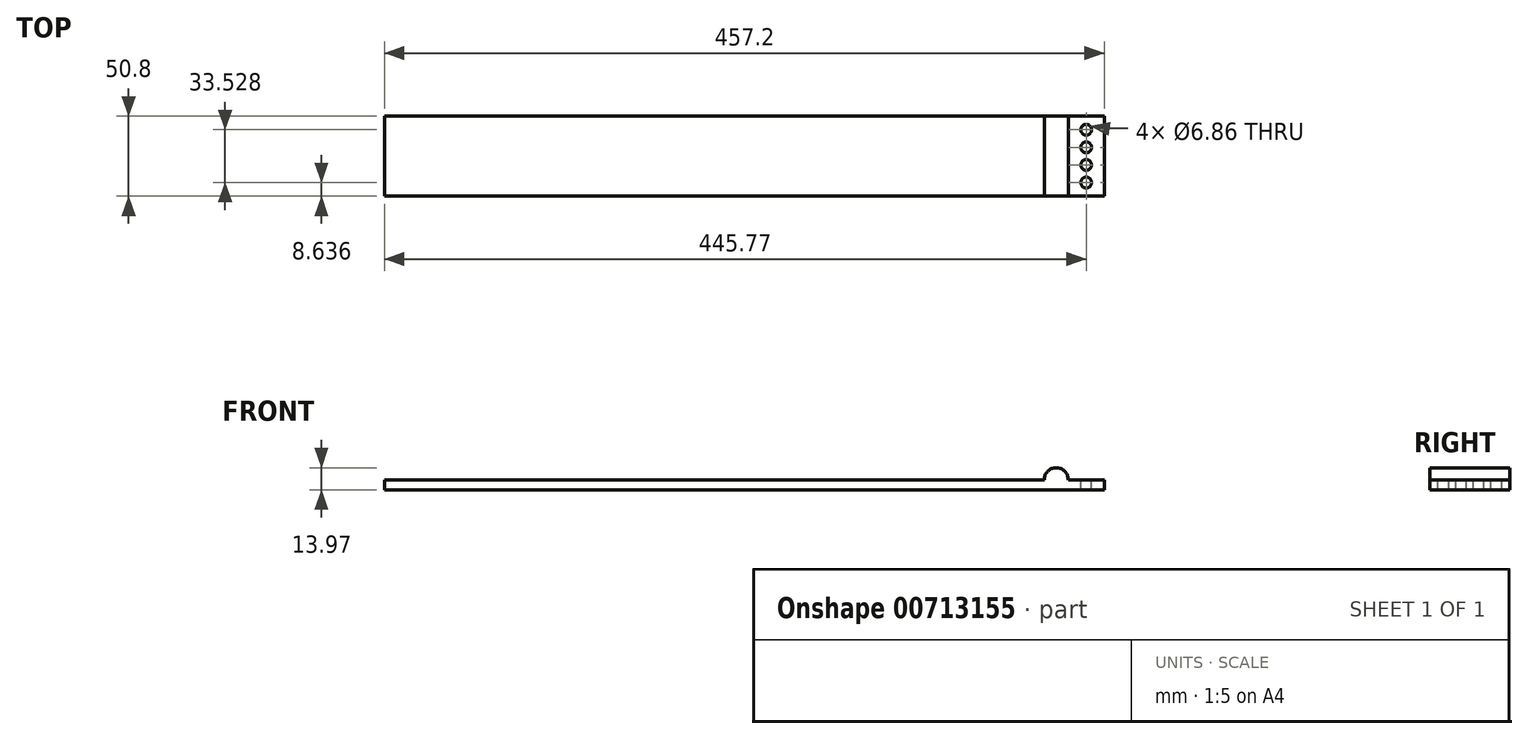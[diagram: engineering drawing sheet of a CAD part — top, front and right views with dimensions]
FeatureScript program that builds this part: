
annotation { "Feature Type Name" : "Feature", "Feature Type Description" : "" }
export const myFeature = defineFeature(function(context is Context, id is Id, definition is map)
    precondition{}
    {
        {
            var Q0;
            Q0=qCreatedBy(makeId("Top.planeOp"),FACE);
            var sketch = newSketch(context, id + "F0", { "sketchPlane" : qUnion([Q0])});
            skLineSegment(sketch, "E0.bottom", {"start": v(-228.6, -25.4) * mm, "end": v(228.6, -25.4) * mm});
            skLineSegment(sketch, "E0.top", {"start": v(-228.6, 25.4) * mm, "end": v(228.6, 25.4) * mm});
            skLineSegment(sketch, "E0.left", {"start": v(-228.6, -25.4) * mm, "end": v(-228.6, 25.4) * mm});
            skLineSegment(sketch, "E0.right", {"start": v(228.6, -25.4) * mm, "end": v(228.6, 25.4) * mm});
            skPoint(sketch, "E0.middle", {"position": v(0, 0) * mm});
            skSolve(sketch);
        }
        {
            var Q0;
            Q0 = qSketchRegion(id + "F0", true);
            extrude(context, id + "F1", {"entities" : qUnion([Q0]), "depth" : 6.35 * mm, "offsetDistance" : 25.4 * mm});
        }
        {
            var Q0;
            Q0=makeQuery(id+"F1.opExtrude","SWEPT_FACE",FACE,{"disambiguationData":[OSD([sQuery(id+"F0.wireOp",EDGE,"E0.bottom")])]});
            var sketch = newSketch(context, id + "F2", { "sketchPlane" : qUnion([Q0])});
            skArc(sketch, "E1", {"start": v(205.74, 6.35) * mm, "mid": v(198.12, 13.97) * mm, "end": v(190.5, 6.35) * mm});
            skLineSegment(sketch, "E2", {"start": v(190.5, 6.35) * mm, "end": v(205.74, 6.35) * mm});
            skSolve(sketch);
        }
        {
            var Q0;
            Q0 = qSketchRegion(id + "F2", true);
            extrude(context, id + "F3", {"entities" : qUnion([Q0]), "operationType" : NewBodyOperationType.ADD, "oppositeDirection" : true, "depth" : 50.8 * mm, "offsetDistance" : 25.4 * mm});
        }
        {
            var Q0;
            {var subQ3=sQuery(id+"F0.wireOp",EDGE,"E0.top");var subQ4=sQuery(id+"F0.wireOp",EDGE,"E0.right");var subQ5=sQuery(id+"F0.wireOp",EDGE,"E0.bottom");Q0=makeQuery(id+"F3.boolean.opBoolean","SPLIT",FACE,{"disambiguationData":[TD([makeQuery(id+"F1.opExtrude","SWEPT_FACE",FACE,{"disambiguationData":[OSD([subQ4])]})])],"derivedFrom":makeQuery(id+"F1.opExtrude","CAP_FACE",FACE,{"disambiguationData":[OSD([subQ5,subQ3,sQuery(id+"F0.wireOp",EDGE,"E0.left"),subQ4])],"isStart":false})});}
            var sketch = newSketch(context, id + "F4", { "sketchPlane" : qUnion([Q0])});
            skCircle(sketch, "E3", {"center": v(217.17, -16.76) * mm, "radius": 3.43 * mm});
            skCircle(sketch, "E4.1.0.0", {"center": v(217.17, -5.59) * mm, "radius": 3.43 * mm});
            skCircle(sketch, "E4.2.0.0", {"center": v(217.17, 5.59) * mm, "radius": 3.43 * mm});
            skCircle(sketch, "E4.3.0.0", {"center": v(217.17, 16.76) * mm, "radius": 3.43 * mm});
            skLineSegment(sketch, "E4.direction1", {"start": v(217.17, -16.76) * mm, "end": v(217.17, -5.59) * mm, "construction": true});
            skLineSegment(sketch, "E5", {"start": v(217.17, 16.76) * mm, "end": v(217.17, 25.4) * mm, "construction": true});
            skLineSegment(sketch, "E6", {"start": v(217.17, -16.76) * mm, "end": v(217.17, -25.4) * mm, "construction": true});
            skSolve(sketch);
        }
        {
            var Q0;
            Q0 = qSketchRegion(id + "F4", true);
            extrude(context, id + "F5", {"entities" : qUnion([Q0]), "operationType" : NewBodyOperationType.REMOVE, "oppositeDirection" : true, "depth" : 25.4 * mm, "offsetDistance" : 25.4 * mm});
        }
    });
